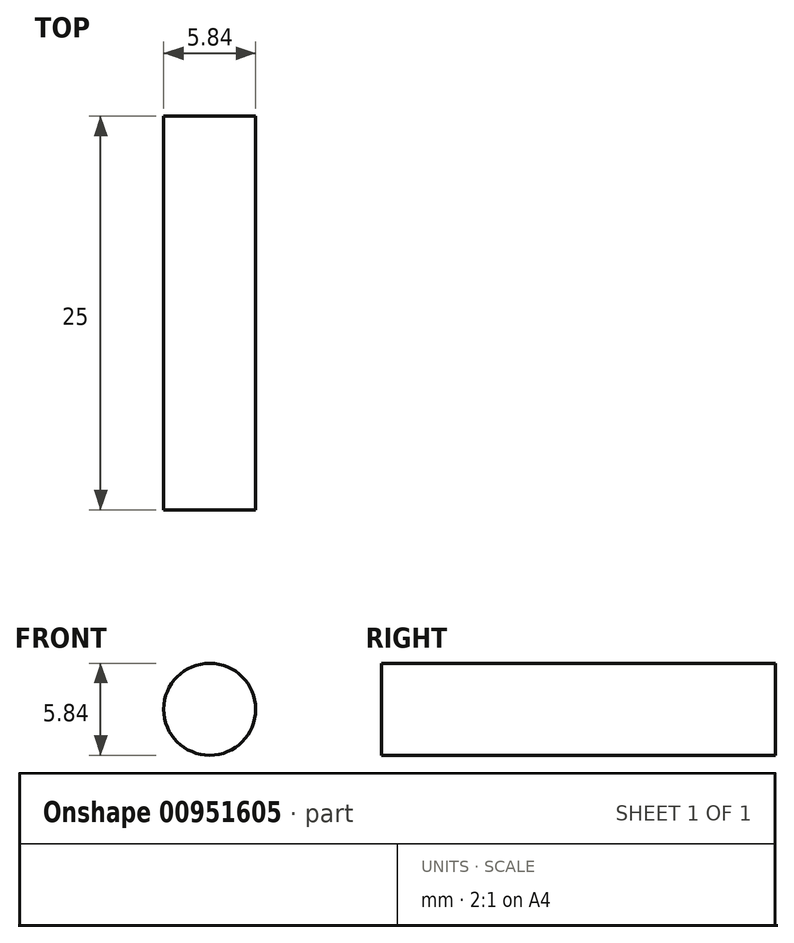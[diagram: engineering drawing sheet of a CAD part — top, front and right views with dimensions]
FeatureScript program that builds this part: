
annotation { "Feature Type Name" : "Feature", "Feature Type Description" : "" }
export const myFeature = defineFeature(function(context is Context, id is Id, definition is map)
    precondition{}
    {
        {
            var Q0;
            Q0=qCreatedBy(makeId("Front.planeOp"),FACE);
            var sketch = newSketch(context, id + "F0", { "sketchPlane" : qUnion([Q0])});
            skCircle(sketch, "E0", {"center": v(0, 0) * mm, "radius": 2.92 * mm});
            skSolve(sketch);
        }
        {
            var Q0;
            Q0 = qSketchRegion(id + "F0", true);
            extrude(context, id + "F1", {"entities" : qUnion([Q0]), "depth" : 25 * mm, "offsetDistance" : 25 * mm});
        }
    });
